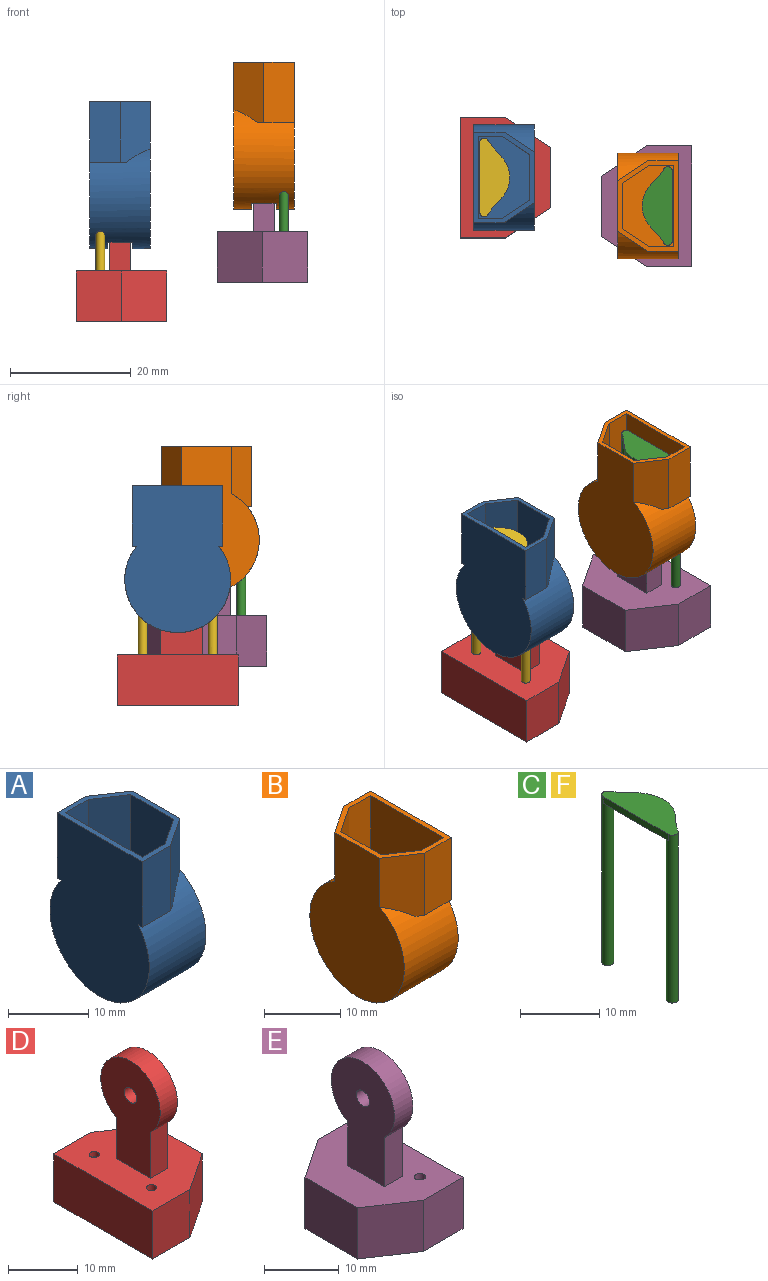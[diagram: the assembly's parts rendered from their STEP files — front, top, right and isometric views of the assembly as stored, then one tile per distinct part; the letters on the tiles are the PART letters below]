
ASSEMBLY  parts=6 mates=2
PART A: 25 faces, bbox 10x17.6x24.3 mm
  f0: cylinder r=8.78mm len=17.56mm, axis (1,0,0), area 333.6mm2, adj f2,f4,f5,f6,f8,f9,f11,f12
  f1: plane 15x10mm, normal (0,0,1), area 30.7mm2, adj f3,f4,f5,f6,f7,f8,f16,f17
  f2: plane 6.06x0.7mm, normal (0,0,-1), area 3.9mm2, adj f0,f3,f4,f8
  f3: plane 10x5mm, normal (0,1,0), area 50mm2, adj f1,f2,f4,f8
  f4: plane 10x5mm, normal (0.55,0.83,0), area 54.3mm2, adj f0,f1,f2,f3,f5
  f5: plane 24.34x17.56mm, normal (1,0,0), area 301.5mm2, adj f0,f1,f4,f6
  f6: plane 10x5mm, normal (0.55,-0.83,0), area 54.3mm2, adj f0,f1,f5,f7,f9
  f7: plane 10x5mm, normal (0,-1,0), area 50mm2, adj f1,f6,f8,f9
  f8: plane 24.34x17.56mm, normal (-1,0,0), area 361.7mm2, adj f0,f1,f2,f3,f7,f9
  f9: plane 6.06x0.7mm, normal (0,0,-1), area 3.9mm2, adj f0,f6,f7,f8
  f10: cylinder r=6.25mm len=12.5mm, axis (1,0,0), area 100.2mm2, adj f11,f12,f14,f15
  f11: plane 4x3.02mm, normal (0,1,-0.01), area 12.1mm2, adj f0,f10,f14,f15
  f12: plane 4x2.53mm, normal (0,0,-1), area 10.1mm2, adj f0,f10,f14,f15
  f13: cylinder r=1.12mm len=4mm, axis (1,0,0), area 28.3mm2, adj f14,f15
  f14: plane 15.03x15.03mm, normal (1,0,0), area 159.5mm2, adj f0,f10,f11,f12,f13
  f15: plane 15.03x15.03mm, normal (-1,0,0), area 159.5mm2, adj f0,f10,f11,f12,f13
  f16: plane 9x4.05mm, normal (0,1,0), area 36.5mm2, adj f1,f17,f21,f22
  f17: plane 9x4.52mm, normal (-0.55,0.83,0), area 48.9mm2, adj f1,f16,f18,f22
  f18: plane 9x7.55mm, normal (-1,0,0), area 67.9mm2, adj f1,f17,f19,f22
  f19: plane 9x4.52mm, normal (-0.55,-0.83,0), area 48.9mm2, adj f1,f18,f20,f22
  f20: plane 9x4.05mm, normal (0,-1,0), area 36.5mm2, adj f1,f19,f21,f22
  f21: plane 13.57x9mm, normal (1,0,0), area 122.1mm2, adj f1,f16,f20,f22
  f22: plane 13.57x8.57mm, normal (0,0,1), area 99.1mm2, adj f16,f17,f18,f19,f20,f21,f23,f24
  f23: cylinder r=0.75mm len=13.75mm, axis (0,0,1), area 61.9mm2, adj f0,f22
  f24: cylinder r=0.75mm len=13.75mm, axis (0,0,1), area 61.9mm2, adj f0,f22
PART B: 25 faces, bbox 10x17.6x24.3 mm
  f0: cylinder r=8.78mm len=17.56mm, axis (-1,0,0), area 333.6mm2, adj f2,f4,f5,f6,f8,f9,f11,f12
  f1: plane 15x10mm, normal (0,0,1), area 30.7mm2, adj f3,f4,f5,f6,f7,f8,f16,f17
  f2: plane 6.06x0.7mm, normal (0,0,-1), area 3.9mm2, adj f0,f3,f4,f8
  f3: plane 10x5mm, normal (0,1,0), area 50mm2, adj f1,f2,f4,f8
  f4: plane 10x5mm, normal (-0.55,0.83,0), area 54.3mm2, adj f0,f1,f2,f3,f5
  f5: plane 24.34x17.56mm, normal (-1,0,0), area 301.5mm2, adj f0,f1,f4,f6
  f6: plane 10x5mm, normal (-0.55,-0.83,0), area 54.3mm2, adj f0,f1,f5,f7,f9
  f7: plane 10x5mm, normal (0,-1,0), area 50mm2, adj f1,f6,f8,f9
  f8: plane 24.34x17.56mm, normal (1,0,0), area 361.7mm2, adj f0,f1,f2,f3,f7,f9
  f9: plane 6.06x0.7mm, normal (0,0,-1), area 3.9mm2, adj f0,f6,f7,f8
  f10: cylinder r=6.25mm len=12.5mm, axis (-1,0,0), area 100.2mm2, adj f11,f12,f14,f15
  f11: plane 4x3.02mm, normal (0,1,-0.01), area 12.1mm2, adj f0,f10,f14,f15
  f12: plane 4x2.53mm, normal (0,0,-1), area 10.1mm2, adj f0,f10,f14,f15
  f13: cylinder r=1.12mm len=4mm, axis (-1,0,0), area 28.3mm2, adj f14,f15
  f14: plane 15.03x15.03mm, normal (-1,0,0), area 159.5mm2, adj f0,f10,f11,f12,f13
  f15: plane 15.03x15.03mm, normal (1,0,0), area 159.5mm2, adj f0,f10,f11,f12,f13
  f16: plane 9x4.05mm, normal (0,1,0), area 36.5mm2, adj f1,f17,f21,f22
  f17: plane 9x4.52mm, normal (0.55,0.83,0), area 48.9mm2, adj f1,f16,f18,f22
  f18: plane 9x7.55mm, normal (1,0,0), area 67.9mm2, adj f1,f17,f19,f22
  f19: plane 9x4.52mm, normal (0.55,-0.83,0), area 48.9mm2, adj f1,f18,f20,f22
  f20: plane 9x4.05mm, normal (0,-1,0), area 36.5mm2, adj f1,f19,f21,f22
  f21: plane 13.57x9mm, normal (-1,0,0), area 122.1mm2, adj f1,f16,f20,f22
  f22: plane 13.57x8.57mm, normal (0,0,1), area 99.1mm2, adj f16,f17,f18,f19,f20,f21,f23,f24
  f23: cylinder r=0.75mm len=13.75mm, axis (0,0,1), area 61.9mm2, adj f0,f22
  f24: cylinder r=0.75mm len=13.75mm, axis (0,0,1), area 61.9mm2, adj f0,f22
PART C: 12 faces, bbox 5x13.1x26 mm
  f0: cylinder r=0.75mm len=26mm, axis (0,0,-1), area 119.8mm2, adj f1,f4,f7,f8,f11
  f1: plane 1.5x1.5mm, normal (0,0,-1), area 1.8mm2, adj f0
  f2: cylinder r=0.75mm len=26mm, axis (0,0,-1), area 119.8mm2, adj f3,f4,f7,f8,f9
  f3: plane 1.5x1.5mm, normal (0,0,-1), area 1.8mm2, adj f2
  f4: plane 12.25x4.97mm, normal (0,0,-1), area 41.5mm2, adj f0,f2,f5,f6,f7,f9,f10,f11
  f5: plane 1.73x1.55mm, normal (0.74,-0.67,0), area 2.3mm2, adj f4,f8,f9,f10
  f6: plane 1.73x1.55mm, normal (0.74,0.67,0), area 2.3mm2, adj f4,f8,f10,f11
  f7: plane 11.57x1mm, normal (-1,0,0), area 11.6mm2, adj f0,f2,f4,f8
  f8: plane 13.07x4.97mm, normal (0,0,1), area 45mm2, adj f0,f2,f5,f6,f7,f9,f10,f11
  f9: cylinder r=5mm len=1.06mm, axis (0,0,-1), area 1.3mm2, adj f2,f4,f5,f8
  f10: cylinder r=5mm len=6.67mm, axis (0,0,1), area 7.3mm2, adj f4,f5,f6,f8
  f11: cylinder r=5mm len=1.06mm, axis (0,0,-1), area 1.3mm2, adj f0,f4,f6,f8
PART D: 18 faces, bbox 15x20x26.9 mm
  f0: plane 8.07x3.5mm, normal (0,-1,0), area 28.3mm2, adj f2,f3,f4,f12
  f1: plane 7.21x3.5mm, normal (0,1,0), area 25.2mm2, adj f2,f3,f4,f12
  f2: cylinder r=6mm len=12mm, axis (-1,0,0), area 106mm2, adj f0,f1,f3,f4
  f3: plane 18.5x12mm, normal (1,0,0), area 155.7mm2, adj f0,f1,f2,f12,f17
  f4: plane 18.5x12mm, normal (-1,0,0), area 155.7mm2, adj f0,f1,f2,f12,f17
  f5: plane 10x8.4mm, normal (1,0,0), area 84mm2, adj f6,f10,f11,f12
  f6: plane 8.4x7.5mm, normal (0.55,-0.83,0), area 75.7mm2, adj f5,f7,f11,f12
  f7: plane 8.4x7.5mm, normal (0,-1,0), area 63mm2, adj f6,f8,f11,f12
  f8: plane 20x8.4mm, normal (-1,0,0), area 168mm2, adj f7,f9,f11,f12
  f9: plane 8.4x7.5mm, normal (0,1,0), area 63mm2, adj f8,f10,f11,f12
  f10: plane 8.4x7.5mm, normal (0.55,0.83,0), area 75.7mm2, adj f5,f9,f11,f12
  f11: plane 20x15mm, normal (0,0,-1), area 262.5mm2, adj f5,f6,f7,f8,f9,f10
  f12: plane 20x15mm, normal (0,0,1), area 234.8mm2, adj f0,f1,f3,f4,f5,f6,f7,f8
  f13: cylinder r=0.75mm len=1.5mm, axis (0,0,1), area 4.5mm2, adj f12,f14
  f14: cone r=0mm half-angle=59deg, axis (0,0,1), area 2.1mm2, adj f13
  f15: cylinder r=0.75mm len=1.5mm, axis (0,0,1), area 4.5mm2, adj f12,f16
  f16: cone r=0mm half-angle=59deg, axis (0,0,1), area 2.1mm2, adj f15
  f17: cylinder r=1.25mm len=3.5mm, axis (1,0,0), area 27.5mm2, adj f3,f4
PART E: 18 faces, bbox 15x20x26.9 mm
  f0: plane 8.07x3.5mm, normal (0,-1,0), area 28.3mm2, adj f2,f3,f4,f12
  f1: plane 7.21x3.5mm, normal (0,1,0), area 25.2mm2, adj f2,f3,f4,f12
  f2: cylinder r=6mm len=12mm, axis (1,0,0), area 106mm2, adj f0,f1,f3,f4
  f3: plane 18.5x12mm, normal (-1,0,0), area 155.7mm2, adj f0,f1,f2,f12,f17
  f4: plane 18.5x12mm, normal (1,0,0), area 155.7mm2, adj f0,f1,f2,f12,f17
  f5: plane 10x8.4mm, normal (-1,0,0), area 84mm2, adj f6,f10,f11,f12
  f6: plane 8.4x7.5mm, normal (-0.55,-0.83,0), area 75.7mm2, adj f5,f7,f11,f12
  f7: plane 8.4x7.5mm, normal (0,-1,0), area 63mm2, adj f6,f8,f11,f12
  f8: plane 20x8.4mm, normal (1,0,0), area 168mm2, adj f7,f9,f11,f12
  f9: plane 8.4x7.5mm, normal (0,1,0), area 63mm2, adj f8,f10,f11,f12
  f10: plane 8.4x7.5mm, normal (-0.55,0.83,0), area 75.7mm2, adj f5,f9,f11,f12
  f11: plane 20x15mm, normal (0,0,-1), area 262.5mm2, adj f5,f6,f7,f8,f9,f10
  f12: plane 20x15mm, normal (0,0,1), area 234.8mm2, adj f0,f1,f3,f4,f5,f6,f7,f8
  f13: cylinder r=0.75mm len=1.5mm, axis (0,0,1), area 4.5mm2, adj f12,f14
  f14: cone r=0mm half-angle=59deg, axis (0,0,1), area 2.1mm2, adj f13
  f15: cylinder r=0.75mm len=1.5mm, axis (0,0,1), area 4.5mm2, adj f12,f16
  f16: cone r=0mm half-angle=59deg, axis (0,0,1), area 2.1mm2, adj f15
  f17: cylinder r=1.25mm len=3.5mm, axis (-1,0,0), area 27.5mm2, adj f3,f4
PART F: same geometry as C
PLACE A t=(39.3,-103.31,76.81)mm
PLACE B t=(-172.8,-108.05,83.35)mm
PLACE C rot(axis=(0,0,1),180deg) t=(-227.49,-42.68,-68.3)mm
PLACE D t=(39.3,-103.31,76.81)mm
PLACE E t=(-172.8,-108.05,83.35)mm
PLACE F t=(93.98,41.03,-74.84)mm
MATE slider C.f2 <-> B.f24  axis (0,0,-1) through (-51.53,2.59,-73.77)mm
MATE slider F.f0 <-> A.f24  axis (0,0,-1) through (-81.97,7.33,-80.31)mm
